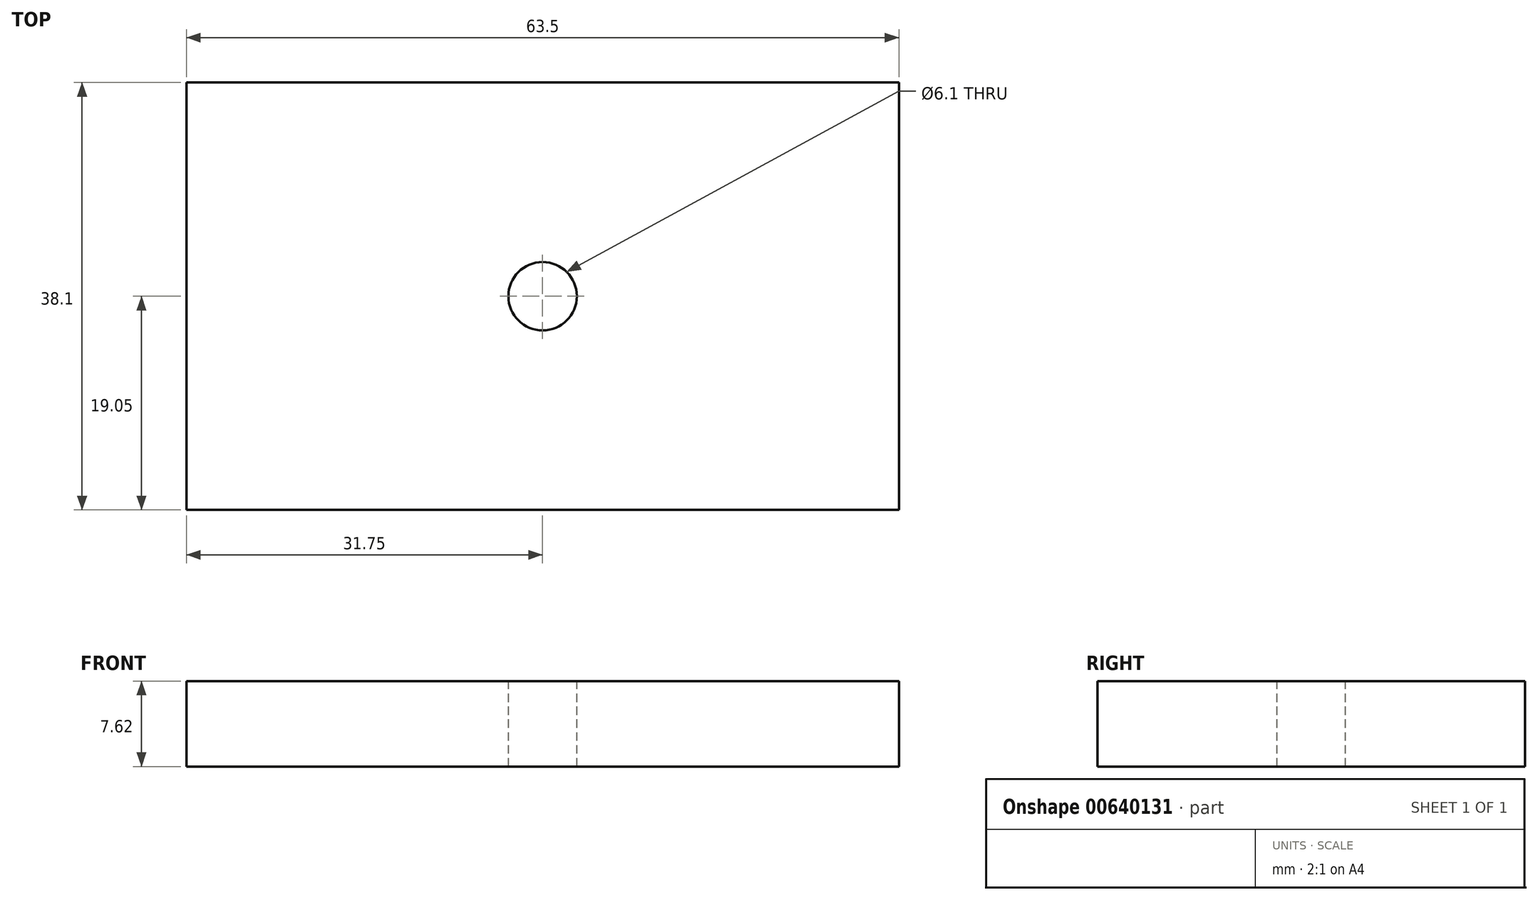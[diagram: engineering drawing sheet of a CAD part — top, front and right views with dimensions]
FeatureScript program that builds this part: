
annotation { "Feature Type Name" : "Feature", "Feature Type Description" : "" }
export const myFeature = defineFeature(function(context is Context, id is Id, definition is map)
    precondition{}
    {
        {
            var Q0;
            Q0=qCreatedBy(makeId("Top.planeOp"),FACE);
            var sketch = newSketch(context, id + "F0", { "sketchPlane" : qUnion([Q0])});
            skPoint(sketch, "E0.middle", {"position": v(0, 0) * mm});
            skLineSegment(sketch, "E1.bottom", {"start": v(31.75, -19.05) * mm, "end": v(-31.75, -19.05) * mm});
            skLineSegment(sketch, "E1.top", {"start": v(31.75, 19.05) * mm, "end": v(-31.75, 19.05) * mm});
            skLineSegment(sketch, "E1.left", {"start": v(31.75, -19.05) * mm, "end": v(31.75, 19.05) * mm});
            skLineSegment(sketch, "E1.right", {"start": v(-31.75, -19.05) * mm, "end": v(-31.75, 19.05) * mm});
            skSolve(sketch);
        }
        {
            var Q0;
            Q0 = qSketchRegion(id + "F0", true);
            extrude(context, id + "F1", {"entities" : qUnion([Q0]), "depth" : 7.62 * mm, "offsetDistance" : 25.4 * mm});
        }
        {
            var Q0;
            Q0=makeQuery(id+"F1.opExtrude","CAP_FACE",FACE,{"disambiguationData":[OSD([sQuery(id+"F0.wireOp",EDGE,"E1.bottom"),sQuery(id+"F0.wireOp",EDGE,"E1.top"),sQuery(id+"F0.wireOp",EDGE,"E1.left"),sQuery(id+"F0.wireOp",EDGE,"E1.right")])],"isStart":false});
            var sketch = newSketch(context, id + "F2", { "sketchPlane" : qUnion([Q0])});
            skCircle(sketch, "E2", {"center": v(0, 0) * mm, "radius": 3.05 * mm});
            skSolve(sketch);
        }
        {
            var Q0;
            Q0=makeQuery(id+"F2.imprint","IMPRINT",FACE,{"disambiguationData":[TD([[makeQuery(id+"F2.imprint","IMPRINT",EDGE,{"derivedFrom":sQuery(id+"F2.wireOp",EDGE,"E2")}),1.0]])]});
            extrude(context, id + "F3", {"entities" : qUnion([Q0]), "operationType" : NewBodyOperationType.REMOVE, "oppositeDirection" : true, "depth" : 25.4 * mm, "offsetDistance" : 25.4 * mm});
        }
    });
